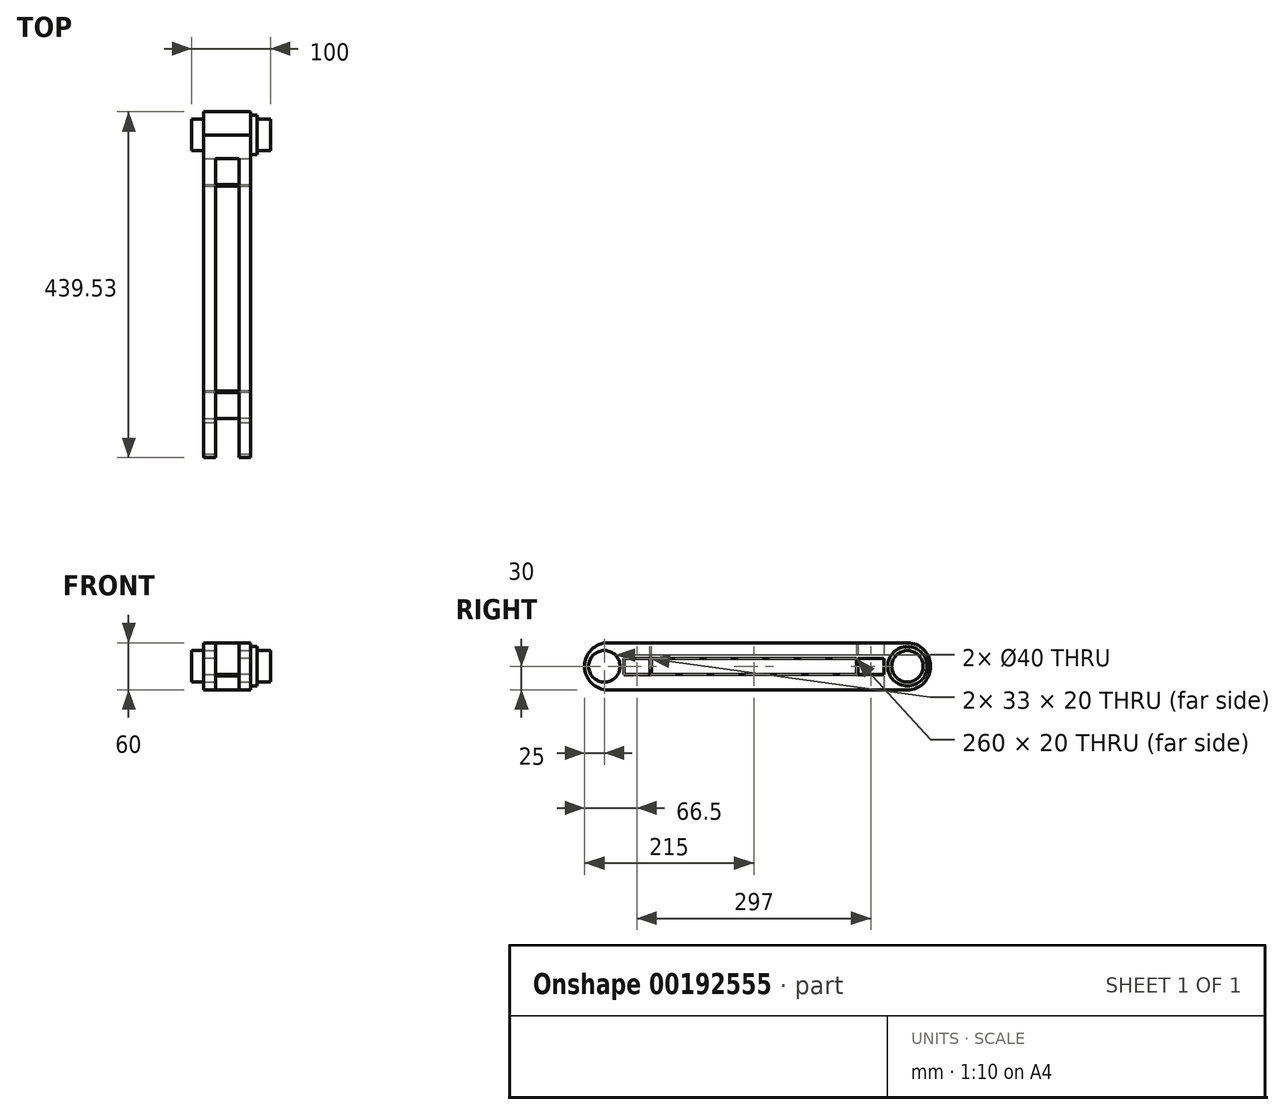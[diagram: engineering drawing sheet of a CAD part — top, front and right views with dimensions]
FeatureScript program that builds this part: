
annotation { "Feature Type Name" : "Feature", "Feature Type Description" : "" }
export const myFeature = defineFeature(function(context is Context, id is Id, definition is map)
    precondition{}
    {
        {
            var Q0;
            Q0=qCreatedBy(makeId("Right.planeOp"),FACE);
            var sketch = newSketch(context, id + "F0", { "sketchPlane" : qUnion([Q0])});
            skCircle(sketch, "E0", {"center": v(0, 0) * mm, "radius": 20 * mm});
            skSolve(sketch);
        }
        {
            var Q0;
            Q0=qSketchRegion(id+"F0",true);
            extrude(context, id + "F1", {"entities" : qUnion([Q0]), "depth" : 100 * mm});
        }
        {
            var Q0;
            Q0=qCreatedBy(makeId("Front.planeOp"),FACE);
            var sketch = newSketch(context, id + "F2", { "sketchPlane" : qUnion([Q0])});
            skLineSegment(sketch, "E1.bottom", {"start": v(15, 30) * mm, "end": v(75, 30) * mm});
            skLineSegment(sketch, "E1.top", {"start": v(15, -30) * mm, "end": v(75, -30) * mm});
            skLineSegment(sketch, "E1.left", {"start": v(15, 30) * mm, "end": v(15, -30) * mm});
            skLineSegment(sketch, "E1.right", {"start": v(75, 30) * mm, "end": v(75, -30) * mm});
            skSolve(sketch);
        }
        {
            var Q0;
            Q0=qSketchRegion(id+"F2",true);
            extrude(context, id + "F3", {"entities" : qUnion([Q0]), "operationType" : NewBodyOperationType.ADD, "depth" : 30 * mm, "hasSecondDirection" : true, "secondDirectionOppositeDirection" : true, "secondDirectionDepth" : 40 * mm});
        }
        {
            var Q0;
            Q0=makeQuery(id+"F3.opExtrude","CAP_FACE",FACE,{"disambiguationData":[OSD([sQuery(id+"F2.wireOp",EDGE,"E1.bottom"),sQuery(id+"F2.wireOp",EDGE,"E1.top"),sQuery(id+"F2.wireOp",EDGE,"E1.left"),sQuery(id+"F2.wireOp",EDGE,"E1.right")])],"isStart":false});
            var sketch = newSketch(context, id + "F4", { "sketchPlane" : qUnion([Q0])});
            skLineSegment(sketch, "E2.bottom", {"start": v(60, 30) * mm, "end": v(75, 30) * mm});
            skLineSegment(sketch, "E2.top", {"start": v(60, 10) * mm, "end": v(75, 10) * mm});
            skLineSegment(sketch, "E2.left", {"start": v(60, 30) * mm, "end": v(60, 10) * mm});
            skLineSegment(sketch, "E2.right", {"start": v(75, 30) * mm, "end": v(75, 10) * mm});
            skLineSegment(sketch, "E3.bottom", {"start": v(15, 30) * mm, "end": v(30, 30) * mm});
            skLineSegment(sketch, "E3.top", {"start": v(15, 10) * mm, "end": v(30, 10) * mm});
            skLineSegment(sketch, "E3.left", {"start": v(15, 30) * mm, "end": v(15, 10) * mm});
            skLineSegment(sketch, "E3.right", {"start": v(30, 30) * mm, "end": v(30, 10) * mm});
            skLineSegment(sketch, "E4.bottom", {"start": v(15, -10) * mm, "end": v(30, -10) * mm});
            skLineSegment(sketch, "E4.top", {"start": v(15, -30) * mm, "end": v(30, -30) * mm});
            skLineSegment(sketch, "E4.left", {"start": v(15, -10) * mm, "end": v(15, -30) * mm});
            skLineSegment(sketch, "E4.right", {"start": v(30, -10) * mm, "end": v(30, -30) * mm});
            skLineSegment(sketch, "E5.bottom", {"start": v(60, -10) * mm, "end": v(75, -10) * mm});
            skLineSegment(sketch, "E5.top", {"start": v(60, -30) * mm, "end": v(75, -30) * mm});
            skLineSegment(sketch, "E5.left", {"start": v(60, -10) * mm, "end": v(60, -30) * mm});
            skLineSegment(sketch, "E5.right", {"start": v(75, -10) * mm, "end": v(75, -30) * mm});
            skSolve(sketch);
        }
        {
            var Q0;
            Q0=qSketchRegion(id+"F4",true);
            extrude(context, id + "F5", {"entities" : qUnion([Q0]), "operationType" : NewBodyOperationType.ADD, "depth" : 380 * mm});
        }
        {
            var Q0;
            Q0=makeQuery(id+"F5.boolean.opBoolean","MERGE",FACE,{"derivedFrom":[makeQuery(id+"F3.opExtrude","SWEPT_FACE",FACE,{"disambiguationData":[OSD([sQuery(id+"F2.wireOp",EDGE,"E1.bottom")])]}),makeQuery(id+"F5.opExtrude","SWEPT_FACE",FACE,{"disambiguationData":[OSD([sQuery(id+"F4.wireOp",EDGE,"E2.bottom")])]}),makeQuery(id+"F5.opExtrude","SWEPT_FACE",FACE,{"disambiguationData":[OSD([sQuery(id+"F4.wireOp",EDGE,"E3.bottom")])]})]});
            var sketch = newSketch(context, id + "F6", { "sketchPlane" : qUnion([Q0])});
            skLineSegment(sketch, "E6.bottom", {"start": v(75, -410) * mm, "end": v(60, -410) * mm});
            skLineSegment(sketch, "E6.top", {"start": v(75, -360) * mm, "end": v(60, -360) * mm});
            skLineSegment(sketch, "E6.left", {"start": v(75, -410) * mm, "end": v(75, -360) * mm});
            skLineSegment(sketch, "E6.right", {"start": v(60, -410) * mm, "end": v(60, -360) * mm});
            skLineSegment(sketch, "E7.bottom", {"start": v(15, -410) * mm, "end": v(30, -410) * mm});
            skLineSegment(sketch, "E7.top", {"start": v(15, -360) * mm, "end": v(30, -360) * mm});
            skLineSegment(sketch, "E7.left", {"start": v(15, -410) * mm, "end": v(15, -360) * mm});
            skLineSegment(sketch, "E7.right", {"start": v(30, -410) * mm, "end": v(30, -360) * mm});
            skSolve(sketch);
        }
        {
            var Q0;
            Q0=qSketchRegion(id+"F6",true);
            extrude(context, id + "F7", {"entities" : qUnion([Q0]), "operationType" : NewBodyOperationType.ADD, "oppositeDirection" : true, "depth" : 50 * mm});
        }
        {
            var Q0;
            Q0=makeQuery(id+"F7.boolean.opBoolean","MERGE",FACE,{"derivedFrom":[makeQuery(id+"F5.boolean.opBoolean","MERGE",FACE,{"derivedFrom":[makeQuery(id+"F3.opExtrude","SWEPT_FACE",FACE,{"disambiguationData":[OSD([sQuery(id+"F2.wireOp",EDGE,"E1.right")])]}),makeQuery(id+"F5.opExtrude","SWEPT_FACE",FACE,{"disambiguationData":[OSD([sQuery(id+"F4.wireOp",EDGE,"E2.right")])]}),makeQuery(id+"F5.opExtrude","SWEPT_FACE",FACE,{"disambiguationData":[OSD([sQuery(id+"F4.wireOp",EDGE,"E5.right")])]})]}),makeQuery(id+"F7.opExtrude","SWEPT_FACE",FACE,{"disambiguationData":[OSD([sQuery(id+"F6.wireOp",EDGE,"E6.left")])]})]});
            var sketch = newSketch(context, id + "F8", { "sketchPlane" : qUnion([Q0])});
            skCircle(sketch, "E8", {"center": v(-385, 0) * mm, "radius": 20 * mm});
            skSolve(sketch);
        }
        {
            var Q0;
            Q0=qSketchRegion(id+"F8",true);
            extrude(context, id + "F9", {"entities" : qUnion([Q0]), "operationType" : NewBodyOperationType.REMOVE, "endBound" : BoundingType.THROUGH_ALL, "oppositeDirection" : true, "depth" : 25 * mm});
        }
        {
            var Q0;
            Q0=makeQuery(id+"F7.boolean.opBoolean","MERGE",FACE,{"derivedFrom":[makeQuery(id+"F5.boolean.opBoolean","MERGE",FACE,{"derivedFrom":[makeQuery(id+"F3.opExtrude","SWEPT_FACE",FACE,{"disambiguationData":[OSD([sQuery(id+"F2.wireOp",EDGE,"E1.right")])]}),makeQuery(id+"F5.opExtrude","SWEPT_FACE",FACE,{"disambiguationData":[OSD([sQuery(id+"F4.wireOp",EDGE,"E2.right")])]}),makeQuery(id+"F5.opExtrude","SWEPT_FACE",FACE,{"disambiguationData":[OSD([sQuery(id+"F4.wireOp",EDGE,"E5.right")])]})]}),makeQuery(id+"F7.opExtrude","SWEPT_FACE",FACE,{"disambiguationData":[OSD([sQuery(id+"F6.wireOp",EDGE,"E6.left")])]})]});
            var sketch = newSketch(context, id + "F10", { "sketchPlane" : qUnion([Q0])});
            skArc(sketch, "E9", {"start": v(-380, 30) * mm, "mid": v(-410, 0) * mm, "end": v(-380, -30) * mm});
            skLineSegment(sketch, "E10", {"start": v(-380, 30) * mm, "end": v(-431.15, 30) * mm});
            skLineSegment(sketch, "E11", {"start": v(-380, -30) * mm, "end": v(-431.15, -30) * mm});
            skLineSegment(sketch, "E12", {"start": v(-431.15, 30) * mm, "end": v(-431.15, -30) * mm});
            skSolve(sketch);
        }
        {
            var Q0;
            Q0 = qSketchRegion(id + "F10", true);
            extrude(context, id + "F11", {"entities" : qUnion([Q0]), "operationType" : NewBodyOperationType.REMOVE, "endBound" : BoundingType.THROUGH_ALL, "oppositeDirection" : true, "depth" : 25 * mm});
        }
        {
            var Q0;
            Q0=qCreatedBy(makeId("Right.planeOp"),FACE);
            var sketch = newSketch(context, id + "F12", { "sketchPlane" : qUnion([Q0])});
            skArc(sketch, "E13", {"start": v(0, -30) * mm, "mid": v(29.53, 0) * mm, "end": v(0, 30) * mm});
            skLineSegment(sketch, "E14", {"start": v(0, 30) * mm, "end": v(49.95, 52.14) * mm});
            skLineSegment(sketch, "E15", {"start": v(49.95, 52.14) * mm, "end": v(73.06, -5) * mm});
            skLineSegment(sketch, "E16", {"start": v(73.06, -5) * mm, "end": v(38.26, -57.71) * mm});
            skLineSegment(sketch, "E17", {"start": v(38.26, -57.71) * mm, "end": v(0, -30) * mm});
            skSolve(sketch);
        }
        {
            var Q0;
            Q0 = qSketchRegion(id + "F12", true);
            extrude(context, id + "F13", {"entities" : qUnion([Q0]), "operationType" : NewBodyOperationType.REMOVE, "endBound" : BoundingType.THROUGH_ALL, "depth" : 25 * mm});
        }
        {
            var Q0;
            Q0=makeQuery(id+"F7.boolean.opBoolean","MERGE",FACE,{"derivedFrom":[makeQuery(id+"F5.boolean.opBoolean","MERGE",FACE,{"derivedFrom":[makeQuery(id+"F3.opExtrude","SWEPT_FACE",FACE,{"disambiguationData":[OSD([sQuery(id+"F2.wireOp",EDGE,"E1.right")])]}),makeQuery(id+"F5.opExtrude","SWEPT_FACE",FACE,{"disambiguationData":[OSD([sQuery(id+"F4.wireOp",EDGE,"E2.right")])]}),makeQuery(id+"F5.opExtrude","SWEPT_FACE",FACE,{"disambiguationData":[OSD([sQuery(id+"F4.wireOp",EDGE,"E5.right")])]})]}),makeQuery(id+"F7.opExtrude","SWEPT_FACE",FACE,{"disambiguationData":[OSD([sQuery(id+"F6.wireOp",EDGE,"E6.left")])]})]});
            var sketch = newSketch(context, id + "F14", { "sketchPlane" : qUnion([Q0])});
            skCircle(sketch, "E18", {"center": v(0, 0) * mm, "radius": 25 * mm});
            skSolve(sketch);
        }
        {
            var Q0;
            Q0 = qSketchRegion(id + "F14", true);
            extrude(context, id + "F15", {"entities" : qUnion([Q0]), "operationType" : NewBodyOperationType.ADD, "depth" : 8 * mm});
        }
        {
            var Q0;
            Q0=makeQuery(id+"F5.opExtrude","SWEPT_FACE",FACE,{"disambiguationData":[OSD([sQuery(id+"F4.wireOp",EDGE,"E5.bottom")])]});
            var sketch = newSketch(context, id + "F16", { "sketchPlane" : qUnion([Q0])});
            skLineSegment(sketch, "E19.bottom", {"start": v(75, -65) * mm, "end": v(15, -65) * mm});
            skLineSegment(sketch, "E19.top", {"start": v(75, -30) * mm, "end": v(15, -30) * mm});
            skLineSegment(sketch, "E19.left", {"start": v(75, -65) * mm, "end": v(75, -30) * mm});
            skLineSegment(sketch, "E19.right", {"start": v(15, -65) * mm, "end": v(15, -30) * mm});
            skSolve(sketch);
        }
        {
            var Q0;
            Q0 = qSketchRegion(id + "F16", true);
            extrude(context, id + "F17", {"entities" : qUnion([Q0]), "operationType" : NewBodyOperationType.ADD, "oppositeDirection" : true, "depth" : 2 * mm});
        }
        {
            var Q0;
            Q0=makeQuery(id+"F17.opExtrude","SWEPT_FACE",FACE,{"disambiguationData":[OSD([sQuery(id+"F16.wireOp",EDGE,"E19.bottom")])]});
            var sketch = newSketch(context, id + "F18", { "sketchPlane" : qUnion([Q0])});
            skLineSegment(sketch, "E20.bottom", {"start": v(15, -12) * mm, "end": v(75, -12) * mm});
            skLineSegment(sketch, "E20.top", {"start": v(15, 30) * mm, "end": v(75, 30) * mm});
            skLineSegment(sketch, "E20.left", {"start": v(15, -12) * mm, "end": v(15, 30) * mm});
            skLineSegment(sketch, "E20.right", {"start": v(75, -12) * mm, "end": v(75, 30) * mm});
            skSolve(sketch);
        }
        {
            var Q0;
            Q0 = qSketchRegion(id + "F18", true);
            extrude(context, id + "F19", {"entities" : qUnion([Q0]), "operationType" : NewBodyOperationType.ADD, "oppositeDirection" : true, "depth" : 2 * mm});
        }
        {
            var Q0;
            {var subQ1=sQuery(id+"F16.wireOp",EDGE,"E19.bottom");Q0=makeQuery(id+"F19.boolean.opBoolean","SPLIT",FACE,{"disambiguationData":[TD([makeQuery(id+"F5.opExtrude","SWEPT_FACE",FACE,{"disambiguationData":[OSD([sQuery(id+"F4.wireOp",EDGE,"E2.left")])]})])],"derivedFrom":makeQuery(id+"F17.boolean.opBoolean","MERGE",FACE,{"derivedFrom":[makeQuery(id+"F5.opExtrude","SWEPT_FACE",FACE,{"disambiguationData":[OSD([sQuery(id+"F4.wireOp",EDGE,"E4.bottom")])]}),makeQuery(id+"F5.opExtrude","SWEPT_FACE",FACE,{"disambiguationData":[OSD([sQuery(id+"F4.wireOp",EDGE,"E5.bottom")])]}),makeQuery(id+"F17.opExtrude","CAP_FACE",FACE,{"disambiguationData":[OSD([subQ1,sQuery(id+"F16.wireOp",EDGE,"E19.top"),sQuery(id+"F16.wireOp",EDGE,"E19.left"),sQuery(id+"F16.wireOp",EDGE,"E19.right")])],"isStart":true})]})});}
            var sketch = newSketch(context, id + "F20", { "sketchPlane" : qUnion([Q0])});
            skLineSegment(sketch, "E21.bottom", {"start": v(15, -325) * mm, "end": v(75, -325) * mm});
            skLineSegment(sketch, "E21.top", {"start": v(15, -360) * mm, "end": v(75, -360) * mm});
            skLineSegment(sketch, "E21.left", {"start": v(15, -325) * mm, "end": v(15, -360) * mm});
            skLineSegment(sketch, "E21.right", {"start": v(75, -325) * mm, "end": v(75, -360) * mm});
            skSolve(sketch);
        }
        {
            var Q0;
            Q0 = qSketchRegion(id + "F20", true);
            extrude(context, id + "F21", {"entities" : qUnion([Q0]), "operationType" : NewBodyOperationType.ADD, "oppositeDirection" : true, "depth" : 2 * mm});
        }
        {
            var Q0;
            Q0=makeQuery(id+"F21.opExtrude","SWEPT_FACE",FACE,{"disambiguationData":[OSD([sQuery(id+"F20.wireOp",EDGE,"E21.bottom")])]});
            var sketch = newSketch(context, id + "F22", { "sketchPlane" : qUnion([Q0])});
            skLineSegment(sketch, "E22.bottom", {"start": v(-75, 30) * mm, "end": v(-15, 30) * mm});
            skLineSegment(sketch, "E22.top", {"start": v(-75, -10) * mm, "end": v(-15, -10) * mm});
            skLineSegment(sketch, "E22.left", {"start": v(-75, 30) * mm, "end": v(-75, -10) * mm});
            skLineSegment(sketch, "E22.right", {"start": v(-15, 30) * mm, "end": v(-15, -10) * mm});
            skSolve(sketch);
        }
        {
            var Q0;
            Q0 = qSketchRegion(id + "F22", true);
            extrude(context, id + "F23", {"entities" : qUnion([Q0]), "operationType" : NewBodyOperationType.ADD, "oppositeDirection" : true, "depth" : 2 * mm});
        }
    });
